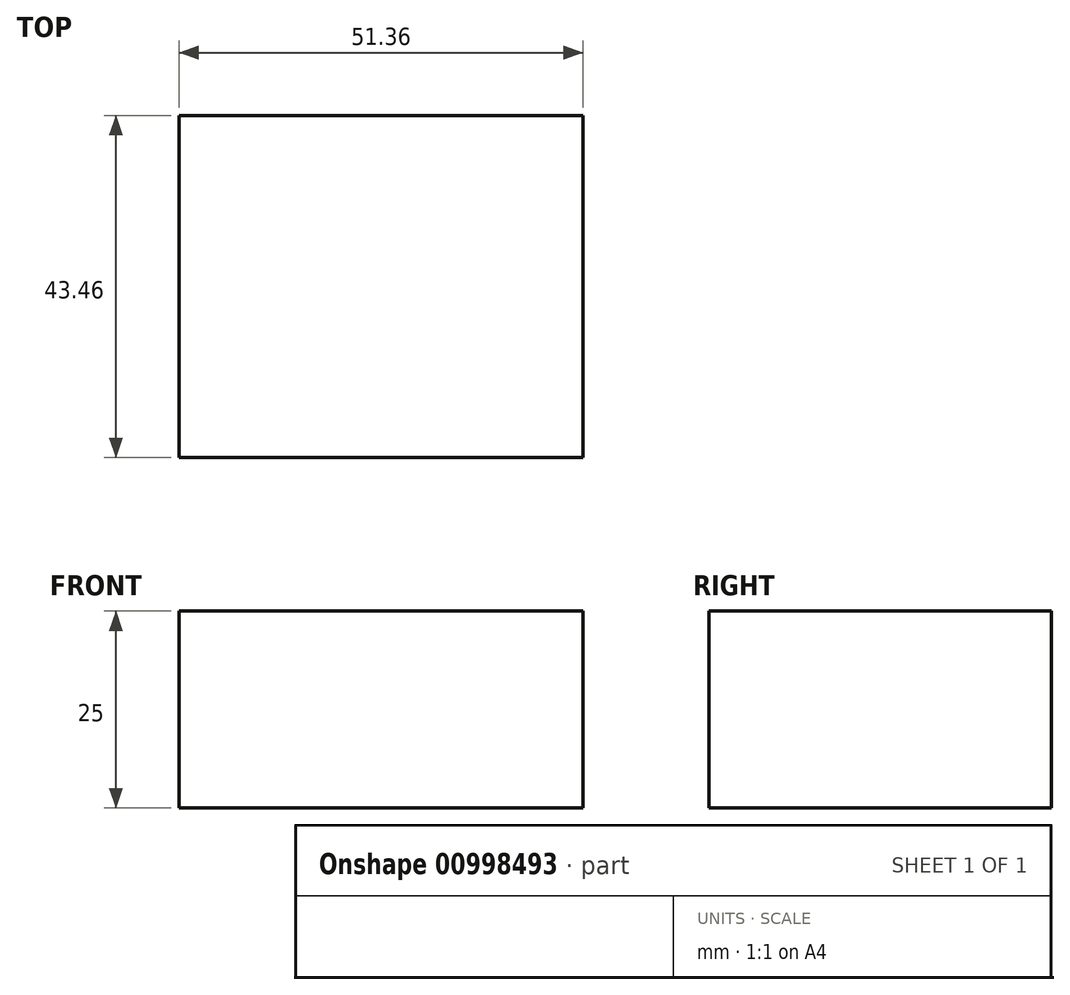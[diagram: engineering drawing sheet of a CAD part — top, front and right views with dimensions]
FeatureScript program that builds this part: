
annotation { "Feature Type Name" : "Feature", "Feature Type Description" : "" }
export const myFeature = defineFeature(function(context is Context, id is Id, definition is map)
    precondition{}
    {
        {
            var Q0;
            Q0=qCreatedBy(makeId("Top.planeOp"),FACE);
            var sketch = newSketch(context, id + "F0", { "sketchPlane" : qUnion([Q0])});
            skLineSegment(sketch, "E0.bottom", {"start": v(25.68, -21.73) * mm, "end": v(-25.68, -21.73) * mm});
            skLineSegment(sketch, "E0.top", {"start": v(25.68, 21.73) * mm, "end": v(-25.68, 21.73) * mm});
            skLineSegment(sketch, "E0.left", {"start": v(25.68, -21.73) * mm, "end": v(25.68, 21.73) * mm});
            skLineSegment(sketch, "E0.right", {"start": v(-25.68, -21.73) * mm, "end": v(-25.68, 21.73) * mm});
            skPoint(sketch, "E0.middle", {"position": v(0, 0) * mm});
            skSolve(sketch);
        }
        {
            var Q0;
            Q0 = qSketchRegion(id + "F0", true);
            extrude(context, id + "F1", {"entities" : qUnion([Q0]), "depth" : 25 * mm, "offsetDistance" : 25 * mm});
        }
    });
